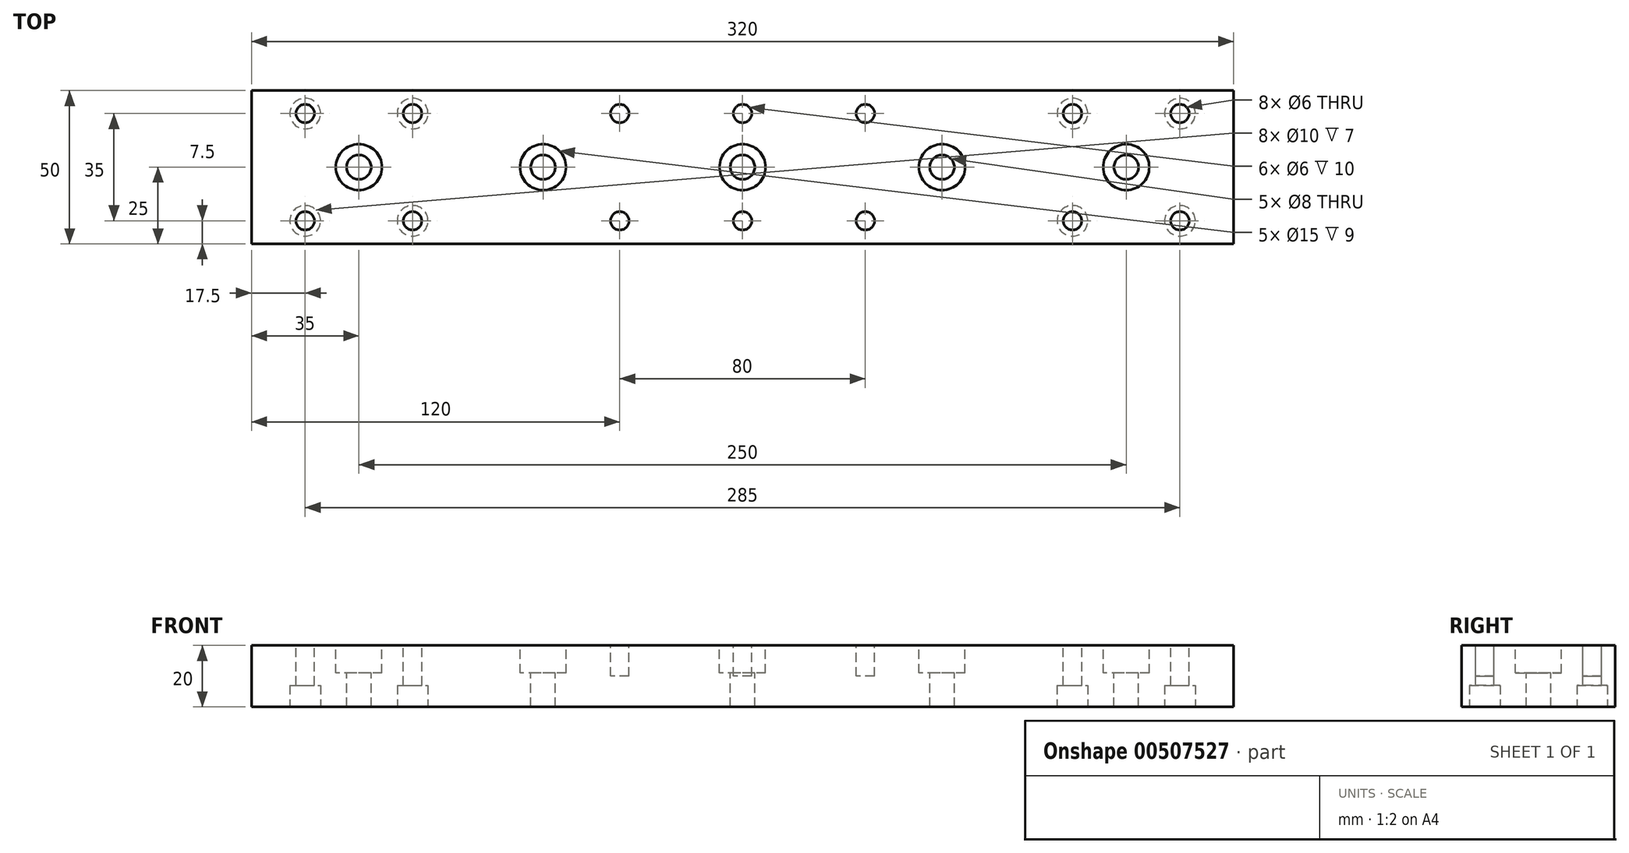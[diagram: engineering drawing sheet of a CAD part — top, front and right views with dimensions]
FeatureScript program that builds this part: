
annotation { "Feature Type Name" : "Feature", "Feature Type Description" : "" }
export const myFeature = defineFeature(function(context is Context, id is Id, definition is map)
    precondition{}
    {
        {
            var Q0;
            Q0=qCreatedBy(makeId("Top.planeOp"),FACE);
            var sketch = newSketch(context, id + "F0", { "sketchPlane" : qUnion([Q0])});
            skLineSegment(sketch, "E0.bottom", {"start": v(0, 0) * mm, "end": v(320, 0) * mm});
            skLineSegment(sketch, "E0.top", {"start": v(0, 50) * mm, "end": v(320, 50) * mm});
            skLineSegment(sketch, "E0.left", {"start": v(0, 0) * mm, "end": v(0, 50) * mm});
            skLineSegment(sketch, "E0.right", {"start": v(320, 0) * mm, "end": v(320, 50) * mm});
            skSolve(sketch);
        }
        {
            var Q0;
            Q0=makeQuery(id+"F0.imprint","IMPRINT",FACE,{"disambiguationData":[TD([[makeQuery(id+"F0.imprint","IMPRINT",EDGE,{"derivedFrom":sQuery(id+"F0.wireOp",EDGE,"E0.bottom")}),1.0]])]});
            extrude(context, id + "F1", {"entities" : qUnion([Q0]), "offsetDistance" : 25 * mm, "depth" : 20 * mm});
        }
        {
            var Q0;
            Q0=makeQuery(id+"F1.opExtrude","CAP_FACE",FACE,{"disambiguationData":[OSD([sQuery(id+"F0.wireOp",EDGE,"E0.bottom"),sQuery(id+"F0.wireOp",EDGE,"E0.top"),sQuery(id+"F0.wireOp",EDGE,"E0.left"),sQuery(id+"F0.wireOp",EDGE,"E0.right")])],"isStart":false});
            var sketch = newSketch(context, id + "F2", { "sketchPlane" : qUnion([Q0])});
            skCircle(sketch, "E1", {"center": v(17.5, 42.5) * mm, "radius": 3 * mm});
            skCircle(sketch, "E2", {"center": v(17.5, 7.5) * mm, "radius": 3 * mm});
            skCircle(sketch, "E3", {"center": v(52.5, 7.5) * mm, "radius": 3 * mm});
            skCircle(sketch, "E4", {"center": v(52.5, 42.5) * mm, "radius": 3 * mm});
            skCircle(sketch, "E5", {"center": v(35, 25) * mm, "radius": 4 * mm});
            skCircle(sketch, "E6", {"center": v(95, 25) * mm, "radius": 4 * mm});
            skCircle(sketch, "E7", {"center": v(160, 25) * mm, "radius": 4 * mm});
            skCircle(sketch, "E8", {"center": v(225, 25) * mm, "radius": 4 * mm});
            skCircle(sketch, "E9", {"center": v(285, 25) * mm, "radius": 4 * mm});
            skCircle(sketch, "E10", {"center": v(267.5, 42.5) * mm, "radius": 3 * mm});
            skCircle(sketch, "E11", {"center": v(302.5, 42.5) * mm, "radius": 3 * mm});
            skCircle(sketch, "E12", {"center": v(302.5, 7.5) * mm, "radius": 3 * mm});
            skCircle(sketch, "E13", {"center": v(267.5, 7.5) * mm, "radius": 3 * mm});
            skSolve(sketch);
        }
        {
            var Q0;
            Q0 = qSketchRegion(id + "F2", true);
            extrude(context, id + "F3", {"entities" : qUnion([Q0]), "operationType" : NewBodyOperationType.REMOVE, "oppositeDirection" : true, "depth" : 20 * mm});
        }
        {
            var Q0;
            Q0=makeQuery(id+"F1.opExtrude","CAP_FACE",FACE,{"disambiguationData":[OSD([sQuery(id+"F0.wireOp",EDGE,"E0.bottom"),sQuery(id+"F0.wireOp",EDGE,"E0.top"),sQuery(id+"F0.wireOp",EDGE,"E0.left"),sQuery(id+"F0.wireOp",EDGE,"E0.right")])],"isStart":false});
            var sketch = newSketch(context, id + "F4", { "sketchPlane" : qUnion([Q0])});
            skCircle(sketch, "E14", {"center": v(35, 25) * mm, "radius": 7.5 * mm});
            skCircle(sketch, "E15", {"center": v(95, 25) * mm, "radius": 7.5 * mm});
            skCircle(sketch, "E16", {"center": v(160, 25) * mm, "radius": 7.5 * mm});
            skCircle(sketch, "E17", {"center": v(225, 25) * mm, "radius": 7.5 * mm});
            skCircle(sketch, "E18", {"center": v(285, 25) * mm, "radius": 7.5 * mm});
            skSolve(sketch);
        }
        {
            var Q0;
            Q0 = qSketchRegion(id + "F4", true);
            extrude(context, id + "F5", {"entities" : qUnion([Q0]), "operationType" : NewBodyOperationType.REMOVE, "oppositeDirection" : true, "depth" : 9 * mm});
        }
        {
            var Q0;
            Q0=makeQuery(id+"F1.opExtrude","CAP_FACE",FACE,{"disambiguationData":[OSD([sQuery(id+"F0.wireOp",EDGE,"E0.bottom"),sQuery(id+"F0.wireOp",EDGE,"E0.top"),sQuery(id+"F0.wireOp",EDGE,"E0.left"),sQuery(id+"F0.wireOp",EDGE,"E0.right")])],"isStart":true});
            var sketch = newSketch(context, id + "F6", { "sketchPlane" : qUnion([Q0])});
            skCircle(sketch, "E19", {"center": v(17.5, -7.5) * mm, "radius": 5 * mm});
            skCircle(sketch, "E20", {"center": v(17.5, -42.5) * mm, "radius": 5 * mm});
            skCircle(sketch, "E21", {"center": v(52.5, -42.5) * mm, "radius": 5 * mm});
            skCircle(sketch, "E22", {"center": v(52.5, -7.5) * mm, "radius": 5 * mm});
            skCircle(sketch, "E23", {"center": v(267.5, -7.5) * mm, "radius": 5 * mm});
            skCircle(sketch, "E24", {"center": v(302.5, -7.5) * mm, "radius": 5 * mm});
            skCircle(sketch, "E25", {"center": v(302.5, -42.5) * mm, "radius": 5 * mm});
            skCircle(sketch, "E26", {"center": v(267.5, -42.5) * mm, "radius": 5 * mm});
            skSolve(sketch);
        }
        {
            var Q0;
            Q0 = qSketchRegion(id + "F6", true);
            extrude(context, id + "F7", {"entities" : qUnion([Q0]), "operationType" : NewBodyOperationType.REMOVE, "oppositeDirection" : true, "depth" : 7 * mm});
        }
        {
            var Q0;
            Q0=makeQuery(id+"F1.opExtrude","CAP_FACE",FACE,{"disambiguationData":[OSD([sQuery(id+"F0.wireOp",EDGE,"E0.bottom"),sQuery(id+"F0.wireOp",EDGE,"E0.top"),sQuery(id+"F0.wireOp",EDGE,"E0.left"),sQuery(id+"F0.wireOp",EDGE,"E0.right")])],"isStart":false});
            var sketch = newSketch(context, id + "F8", { "sketchPlane" : qUnion([Q0])});
            skCircle(sketch, "E27", {"center": v(160, 25) * mm, "radius": 2.5 * mm});
            skCircle(sketch, "E28", {"center": v(160, 7.5) * mm, "radius": 3 * mm});
            skCircle(sketch, "E29", {"center": v(160, 42.5) * mm, "radius": 3 * mm});
            skCircle(sketch, "E30", {"center": v(120, 42.5) * mm, "radius": 3 * mm});
            skCircle(sketch, "E31", {"center": v(120, 7.5) * mm, "radius": 3 * mm});
            skCircle(sketch, "E32", {"center": v(200, 42.5) * mm, "radius": 3 * mm});
            skCircle(sketch, "E33", {"center": v(200, 7.5) * mm, "radius": 3 * mm});
            skSolve(sketch);
        }
        {
            var Q0;
            Q0=makeQuery(id+"F8.imprint","IMPRINT",FACE,{"disambiguationData":[TD([[makeQuery(id+"F8.imprint","IMPRINT",EDGE,{"derivedFrom":sQuery(id+"F8.wireOp",EDGE,"E30")}),1.0]])]});
            var Q1;
            Q1=makeQuery(id+"F8.imprint","IMPRINT",FACE,{"disambiguationData":[TD([[makeQuery(id+"F8.imprint","IMPRINT",EDGE,{"derivedFrom":sQuery(id+"F8.wireOp",EDGE,"E31")}),1.0]])]});
            var Q2;
            Q2=makeQuery(id+"F8.imprint","IMPRINT",FACE,{"disambiguationData":[TD([[makeQuery(id+"F8.imprint","IMPRINT",EDGE,{"derivedFrom":sQuery(id+"F8.wireOp",EDGE,"E29")}),1.0]])]});
            var Q3;
            Q3=makeQuery(id+"F8.imprint","IMPRINT",FACE,{"disambiguationData":[TD([[makeQuery(id+"F8.imprint","IMPRINT",EDGE,{"derivedFrom":sQuery(id+"F8.wireOp",EDGE,"E28")}),1.0]])]});
            var Q4;
            Q4=makeQuery(id+"F8.imprint","IMPRINT",FACE,{"disambiguationData":[TD([[makeQuery(id+"F8.imprint","IMPRINT",EDGE,{"derivedFrom":sQuery(id+"F8.wireOp",EDGE,"E32")}),1.0]])]});
            var Q5;
            Q5=makeQuery(id+"F8.imprint","IMPRINT",FACE,{"disambiguationData":[TD([[makeQuery(id+"F8.imprint","IMPRINT",EDGE,{"derivedFrom":sQuery(id+"F8.wireOp",EDGE,"E33")}),1.0]])]});
            extrude(context, id + "F9", {"entities" : qUnion([Q0, Q1, Q2, Q3, Q4, Q5]), "operationType" : NewBodyOperationType.REMOVE, "oppositeDirection" : true, "depth" : 10 * mm, "offsetDistance" : 25 * mm});
        }
    });
